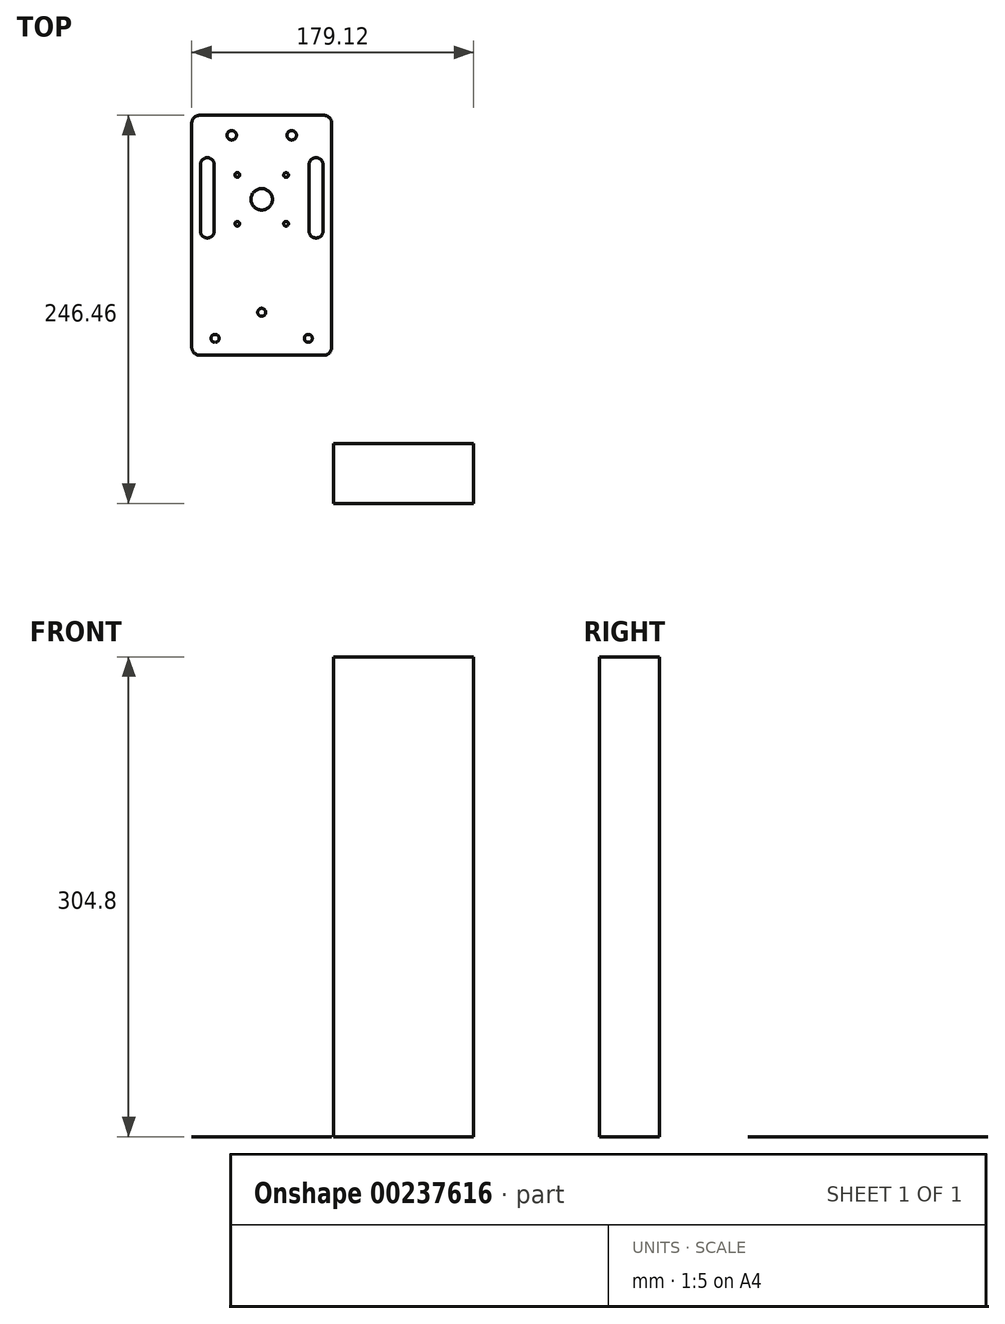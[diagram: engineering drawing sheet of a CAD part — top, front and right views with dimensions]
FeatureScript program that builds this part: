
annotation { "Feature Type Name" : "Feature", "Feature Type Description" : "" }
export const myFeature = defineFeature(function(context is Context, id is Id, definition is map)
    precondition{}
    {
        {
            var Q0;
            Q0=qCreatedBy(makeId("Top.planeOp"),FACE);
            var sketch = newSketch(context, id + "F0", { "sketchPlane" : qUnion([Q0])});
            skLineSegment(sketch, "E0.bottom", {"start": v(-77.92, 133.48) * mm, "end": v(-166.82, 133.48) * mm});
            skLineSegment(sketch, "E0.top", {"start": v(-77.92, 285.88) * mm, "end": v(-166.82, 285.88) * mm});
            skLineSegment(sketch, "E0.left", {"start": v(-77.92, 133.48) * mm, "end": v(-77.92, 285.88) * mm});
            skLineSegment(sketch, "E0.right", {"start": v(-166.82, 133.48) * mm, "end": v(-166.82, 285.88) * mm});
            skPoint(sketch, "E0.middle", {"position": v(-122.37, 209.68) * mm});
            skCircle(sketch, "E1", {"center": v(-141.42, 273.18) * mm, "radius": 3 * mm});
            skCircle(sketch, "E2", {"center": v(-103.32, 273.18) * mm, "radius": 3 * mm});
            skLineSegment(sketch, "E3", {"start": v(-77.92, 273.18) * mm, "end": v(-103.32, 273.18) * mm, "construction": true});
            skLineSegment(sketch, "E4", {"start": v(-166.82, 273.18) * mm, "end": v(-141.42, 273.18) * mm, "construction": true});
            skCircle(sketch, "E5", {"center": v(-122.37, 232.49) * mm, "radius": 6.8 * mm});
            skPoint(sketch, "E5.centerSnap0", {"position": v(-122.37, 171.58) * mm});
            skLineSegment(sketch, "E6.bottom", {"start": v(-137.87, 247.99) * mm, "end": v(-106.87, 247.99) * mm, "construction": true});
            skLineSegment(sketch, "E6.top", {"start": v(-137.87, 216.99) * mm, "end": v(-106.87, 216.99) * mm, "construction": true});
            skLineSegment(sketch, "E6.left", {"start": v(-137.87, 247.99) * mm, "end": v(-137.87, 216.99) * mm, "construction": true});
            skLineSegment(sketch, "E6.right", {"start": v(-106.87, 247.99) * mm, "end": v(-106.87, 216.99) * mm, "construction": true});
            skCircle(sketch, "E7", {"center": v(-137.87, 247.99) * mm, "radius": 1.5 * mm});
            skCircle(sketch, "E8", {"center": v(-137.87, 216.99) * mm, "radius": 1.5 * mm});
            skCircle(sketch, "E9", {"center": v(-106.87, 216.99) * mm, "radius": 1.5 * mm});
            skCircle(sketch, "E10", {"center": v(-106.87, 247.99) * mm, "radius": 1.5 * mm});
            skLineSegment(sketch, "E11", {"start": v(-166.82, 171.58) * mm, "end": v(-77.92, 171.58) * mm, "construction": true});
            skLineSegment(sketch, "E12", {"start": v(-156.9, 254.5) * mm, "end": v(-156.9, 212.4) * mm, "construction": true});
            skLineSegment(sketch, "E13", {"start": v(-87.84, 254.5) * mm, "end": v(-87.84, 212.4) * mm, "construction": true});
            skArc(sketch, "E14.0.startCap", {"start": v(-161.34, 254.5) * mm, "mid": v(-156.9, 258.94) * mm, "end": v(-152.45, 254.5) * mm});
            skArc(sketch, "E14.0.endCap", {"start": v(-152.45, 212.4) * mm, "mid": v(-156.9, 207.95) * mm, "end": v(-161.34, 212.4) * mm});
            skLineSegment(sketch, "E14.0.left", {"start": v(-152.45, 254.5) * mm, "end": v(-152.45, 212.4) * mm});
            skLineSegment(sketch, "E14.0.right", {"start": v(-161.34, 254.5) * mm, "end": v(-161.34, 212.4) * mm});
            skArc(sketch, "E15.0.startCap", {"start": v(-92.28, 254.5) * mm, "mid": v(-87.84, 258.94) * mm, "end": v(-83.4, 254.5) * mm});
            skArc(sketch, "E15.0.endCap", {"start": v(-83.4, 212.4) * mm, "mid": v(-87.84, 207.95) * mm, "end": v(-92.28, 212.4) * mm});
            skLineSegment(sketch, "E15.0.left", {"start": v(-83.4, 254.5) * mm, "end": v(-83.4, 212.4) * mm});
            skLineSegment(sketch, "E15.0.right", {"start": v(-92.28, 254.5) * mm, "end": v(-92.28, 212.4) * mm});
            skLineSegment(sketch, "E16", {"start": v(-87.84, 254.5) * mm, "end": v(-77.92, 254.5) * mm, "construction": true});
            skLineSegment(sketch, "E17", {"start": v(-166.82, 254.5) * mm, "end": v(-156.9, 254.5) * mm, "construction": true});
            skCircle(sketch, "E18", {"center": v(-151.99, 144.2) * mm, "radius": 2.54 * mm});
            skCircle(sketch, "E19", {"center": v(-92.75, 144.2) * mm, "radius": 2.54 * mm});
            skCircle(sketch, "E20", {"center": v(-122.37, 160.73) * mm, "radius": 2.54 * mm});
            skLineSegment(sketch, "E21", {"start": v(-151.99, 144.2) * mm, "end": v(-122.37, 160.73) * mm, "construction": true});
            skLineSegment(sketch, "E22", {"start": v(-122.37, 160.73) * mm, "end": v(-92.75, 144.2) * mm, "construction": true});
            skSolve(sketch);
        }
        {
            var Q0;
            Q0 = qSketchRegion(id + "F0", true);
            extrude(context, id + "F1", {"entities" : qUnion([Q0]), "depth" : 1 / 101.6 * mm});
        }
        {
            var Q0;
            Q0=makeQuery(id+"F1.opExtrude","SWEPT_EDGE",EDGE,{"disambiguationData":[OSD([sQuery(id+"F0.wireOp",EDGE,"E0.top"),sQuery(id+"F0.wireOp",EDGE,"E0.left")])]});
            var Q1;
            Q1=makeQuery(id+"F1.opExtrude","SWEPT_EDGE",EDGE,{"disambiguationData":[OSD([sQuery(id+"F0.wireOp",EDGE,"E0.top"),sQuery(id+"F0.wireOp",EDGE,"E0.right")])]});
            var Q2;
            Q2=makeQuery(id+"F1.opExtrude","SWEPT_EDGE",EDGE,{"disambiguationData":[OSD([sQuery(id+"F0.wireOp",EDGE,"E0.bottom"),sQuery(id+"F0.wireOp",EDGE,"E0.left")])]});
            var Q3;
            Q3=makeQuery(id+"F1.opExtrude","SWEPT_EDGE",EDGE,{"disambiguationData":[OSD([sQuery(id+"F0.wireOp",EDGE,"E0.bottom"),sQuery(id+"F0.wireOp",EDGE,"E0.right")])]});
            fillet(context, id + "F2", {"entities" : qUnion([Q0, Q1, Q2, Q3]), "radius" : 5.08 * mm, "tangentPropagation" : true, "allowEdgeOverflow" : false});
        }
        {
            var Q0;
            Q0=qCreatedBy(makeId("Top.planeOp"),FACE);
            var sketch = newSketch(context, id + "F3", { "sketchPlane" : qUnion([Q0])});
            skLineSegment(sketch, "E23.bottom", {"start": v(12.3, 39.42) * mm, "end": v(-76.6, 39.42) * mm});
            skLineSegment(sketch, "E23.top", {"start": v(12.3, 77.52) * mm, "end": v(-76.6, 77.52) * mm});
            skLineSegment(sketch, "E23.left", {"start": v(12.3, 39.42) * mm, "end": v(12.3, 77.52) * mm});
            skLineSegment(sketch, "E23.right", {"start": v(-76.6, 39.42) * mm, "end": v(-76.6, 77.52) * mm});
            skPoint(sketch, "E23.middle", {"position": v(-32.15, 58.47) * mm});
            skSolve(sketch);
        }
        {
            var Q0;
            Q0=makeQuery(id+"F3.imprint","IMPRINT",FACE,{"disambiguationData":[TD([[makeQuery(id+"F3.imprint","IMPRINT",EDGE,{"derivedFrom":sQuery(id+"F3.wireOp",EDGE,"E23.bottom")}),-1.0]])]});
            extrude(context, id + "F4", {"entities" : qUnion([Q0]), "depth" : 304.8 * mm});
        }
    });
